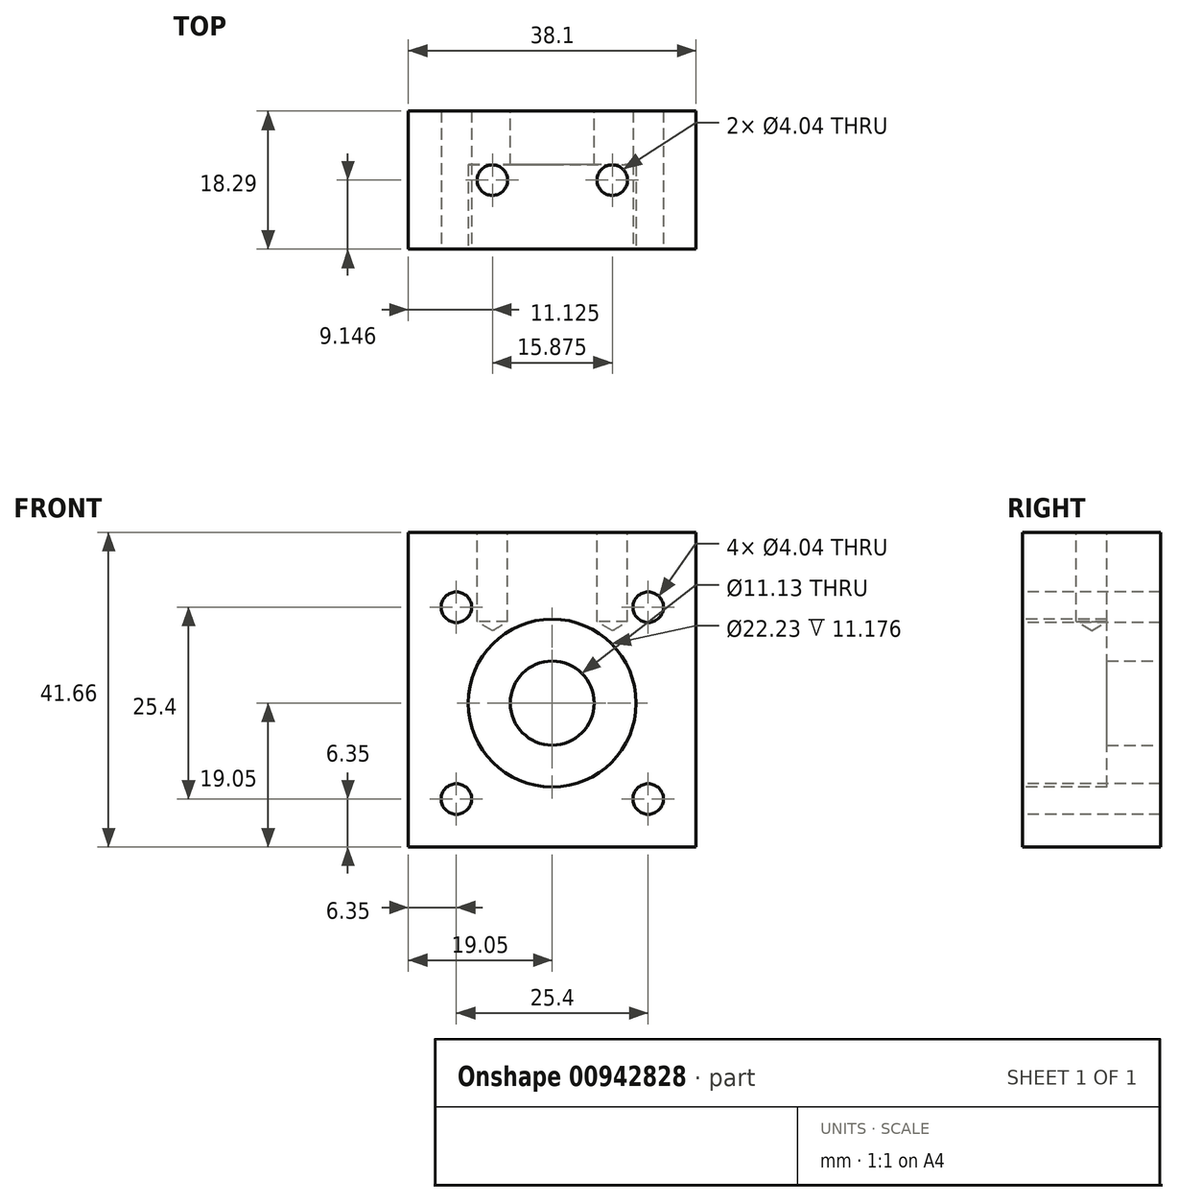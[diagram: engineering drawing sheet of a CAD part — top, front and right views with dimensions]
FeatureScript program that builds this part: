
annotation { "Feature Type Name" : "Feature", "Feature Type Description" : "" }
export const myFeature = defineFeature(function(context is Context, id is Id, definition is map)
    precondition{}
    {
        {
            var Q0;
            Q0=qCreatedBy(makeId("Front.planeOp"),FACE);
            var sketch = newSketch(context, id + "F0", { "sketchPlane" : qUnion([Q0])});
            skLineSegment(sketch, "E0.bottom", {"start": v(-19.05, 19.05) * mm, "end": v(19.05, 19.05) * mm});
            skLineSegment(sketch, "E0.top", {"start": v(-19.05, -19.05) * mm, "end": v(19.05, -19.05) * mm});
            skLineSegment(sketch, "E0.left", {"start": v(-19.05, 19.05) * mm, "end": v(-19.05, -19.05) * mm});
            skLineSegment(sketch, "E0.right", {"start": v(19.05, 19.05) * mm, "end": v(19.05, -19.05) * mm});
            skPoint(sketch, "E0.middle", {"position": v(0, 0) * mm});
            skCircle(sketch, "E1", {"center": v(0, 0) * mm, "radius": 5.56 * mm});
            skSolve(sketch);
        }
        {
            var Q0;
            Q0=makeQuery(id+"F0.imprint","IMPRINT",FACE,{"disambiguationData":[TD([[makeQuery(id+"F0.imprint","IMPRINT",EDGE,{"derivedFrom":sQuery(id+"F0.wireOp",EDGE,"E0.bottom")}),-1.0]])]});
            extrude(context, id + "F1", {"entities" : qUnion([Q0]), "depth" : 18.29 * mm, "offsetDistance" : 25.4 * mm});
        }
        {
            var Q0;
            Q0=makeQuery(id+"F1.opExtrude","CAP_FACE",FACE,{"disambiguationData":[OSD([sQuery(id+"F0.wireOp",EDGE,"E0.bottom"),sQuery(id+"F0.wireOp",EDGE,"E0.top"),sQuery(id+"F0.wireOp",EDGE,"E0.left"),sQuery(id+"F0.wireOp",EDGE,"E0.right"),sQuery(id+"F0.wireOp",EDGE,"E1")])],"isStart":false});
            var sketch = newSketch(context, id + "F2", { "sketchPlane" : qUnion([Q0])});
            skPoint(sketch, "E2", {"position": v(-12.7, -12.7) * mm});
            skPoint(sketch, "E3", {"position": v(-12.7, 12.7) * mm});
            skPoint(sketch, "E4", {"position": v(12.7, 12.7) * mm});
            skPoint(sketch, "E5", {"position": v(12.7, -12.7) * mm});
            skSolve(sketch);
        }
        {
            var Q0;
            Q0=sQuery(id+"F2.wireOp",VERTEX,"E2");
            var Q1;
            Q1=sQuery(id+"F2.wireOp",VERTEX,"E3");
            var Q2;
            Q2=sQuery(id+"F2.wireOp",VERTEX,"E4");
            var Q3;
            Q3=sQuery(id+"F2.wireOp",VERTEX,"E5");
            var Q4;
            Q4=makeQuery(id+"F1.opExtrude","SWEPT_BODY",BODY,{"disambiguationData":[OSD([sQuery(id+"F0.wireOp",EDGE,"E0.bottom"),sQuery(id+"F0.wireOp",EDGE,"E0.top"),sQuery(id+"F0.wireOp",EDGE,"E0.left"),sQuery(id+"F0.wireOp",EDGE,"E0.right"),sQuery(id+"F0.wireOp",EDGE,"E1")])]});
            hole(context, id + "F3", {"style" : HoleStyle.SIMPLE, "endStyle" : HoleEndStyle.THROUGH, "standardTappedOrClearance" : lookupTablePath({ "standard" : "ANSI", "engagement" : "75%", "pitch" : "32 tpi", "size" : "#10", "type" : "Tapped" }), "standardBlindInLast" : lookupTablePath({ "standard" : "ANSI", "fit" : "Normal", "engagement" : "75%", "pitch" : "32 tpi", "size" : "#10", "type" : "Clearance & tapped" }), "holeDiameter" : 4.04 * mm, "majorDiameter" : 4.83 * mm, "showTappedDepth" : true, "isTappedThrough" : true, "tappedDepth" : 18.29 * mm, "tapClearance" : 3, "locations" : qUnion([Q0, Q1, Q2, Q3]), "scope" : qUnion([Q4])});
        }
        {
            var Q0;
            Q0=makeQuery(id+"F1.opExtrude","CAP_FACE",FACE,{"disambiguationData":[OSD([sQuery(id+"F0.wireOp",EDGE,"E0.bottom"),sQuery(id+"F0.wireOp",EDGE,"E0.top"),sQuery(id+"F0.wireOp",EDGE,"E0.left"),sQuery(id+"F0.wireOp",EDGE,"E0.right"),sQuery(id+"F0.wireOp",EDGE,"E1")])],"isStart":false});
            var sketch = newSketch(context, id + "F4", { "sketchPlane" : qUnion([Q0])});
            skCircle(sketch, "E6", {"center": v(0, 0) * mm, "radius": 11.11 * mm});
            skSolve(sketch);
        }
        {
            var Q0;
            Q0=makeQuery(id+"F4.imprint","IMPRINT",FACE,{"disambiguationData":[TD([[makeQuery(id+"F4.imprint","IMPRINT",EDGE,{"derivedFrom":sQuery(id+"F4.wireOp",EDGE,"E6")}),1.0]])]});
            extrude(context, id + "F5", {"entities" : qUnion([Q0]), "operationType" : NewBodyOperationType.REMOVE, "oppositeDirection" : true, "depth" : 11.18 * mm, "offsetDistance" : 25.4 * mm});
        }
        {
            var Q0;
            Q0=makeQuery(id+"F1.opExtrude","SWEPT_FACE",FACE,{"disambiguationData":[OSD([sQuery(id+"F0.wireOp",EDGE,"E0.bottom")])]});
            extrude(context, id + "F6", {"entities" : qUnion([Q0]), "operationType" : NewBodyOperationType.ADD, "depth" : 3.56 * mm, "offsetDistance" : 25.4 * mm});
        }
        {
            var Q0;
            Q0=makeQuery(id+"F6.opExtrude","CAP_FACE",FACE,{"disambiguationData":[OSD([sQuery(id+"F0.wireOp",EDGE,"E0.bottom")])],"isStart":false});
            var sketch = newSketch(context, id + "F7", { "sketchPlane" : qUnion([Q0])});
            skPoint(sketch, "E7", {"position": v(-7.92, -9.14) * mm});
            skPoint(sketch, "E8", {"position": v(7.95, -9.14) * mm});
            skSolve(sketch);
        }
        {
            var Q0;
            Q0=sQuery(id+"F7.wireOp",VERTEX,"E7");
            var Q1;
            Q1=sQuery(id+"F7.wireOp",VERTEX,"E8");
            var Q2;
            Q2=makeQuery(id+"F1.opExtrude","SWEPT_BODY",BODY,{"disambiguationData":[OSD([sQuery(id+"F0.wireOp",EDGE,"E0.bottom"),sQuery(id+"F0.wireOp",EDGE,"E0.top"),sQuery(id+"F0.wireOp",EDGE,"E0.left"),sQuery(id+"F0.wireOp",EDGE,"E0.right"),sQuery(id+"F0.wireOp",EDGE,"E1")])]});
            hole(context, id + "F8", {"style" : HoleStyle.SIMPLE, "endStyle" : HoleEndStyle.BLIND, "standardTappedOrClearance" : lookupTablePath({ "standard" : "ANSI", "engagement" : "75%", "pitch" : "32 tpi", "size" : "#10", "type" : "Tapped" }), "standardBlindInLast" : lookupTablePath({ "standard" : "ANSI", "fit" : "Normal", "engagement" : "75%", "pitch" : "32 tpi", "size" : "#10", "type" : "Clearance & tapped" }), "holeDiameter" : 4.04 * mm, "majorDiameter" : 4.83 * mm, "showTappedDepth" : true, "holeDepth" : 11.8 * mm, "isTappedThrough" : true, "tappedDepth" : 9.43 * mm, "tapClearance" : 3, "locations" : qUnion([Q0, Q1]), "scope" : qUnion([Q2])});
        }
    });
